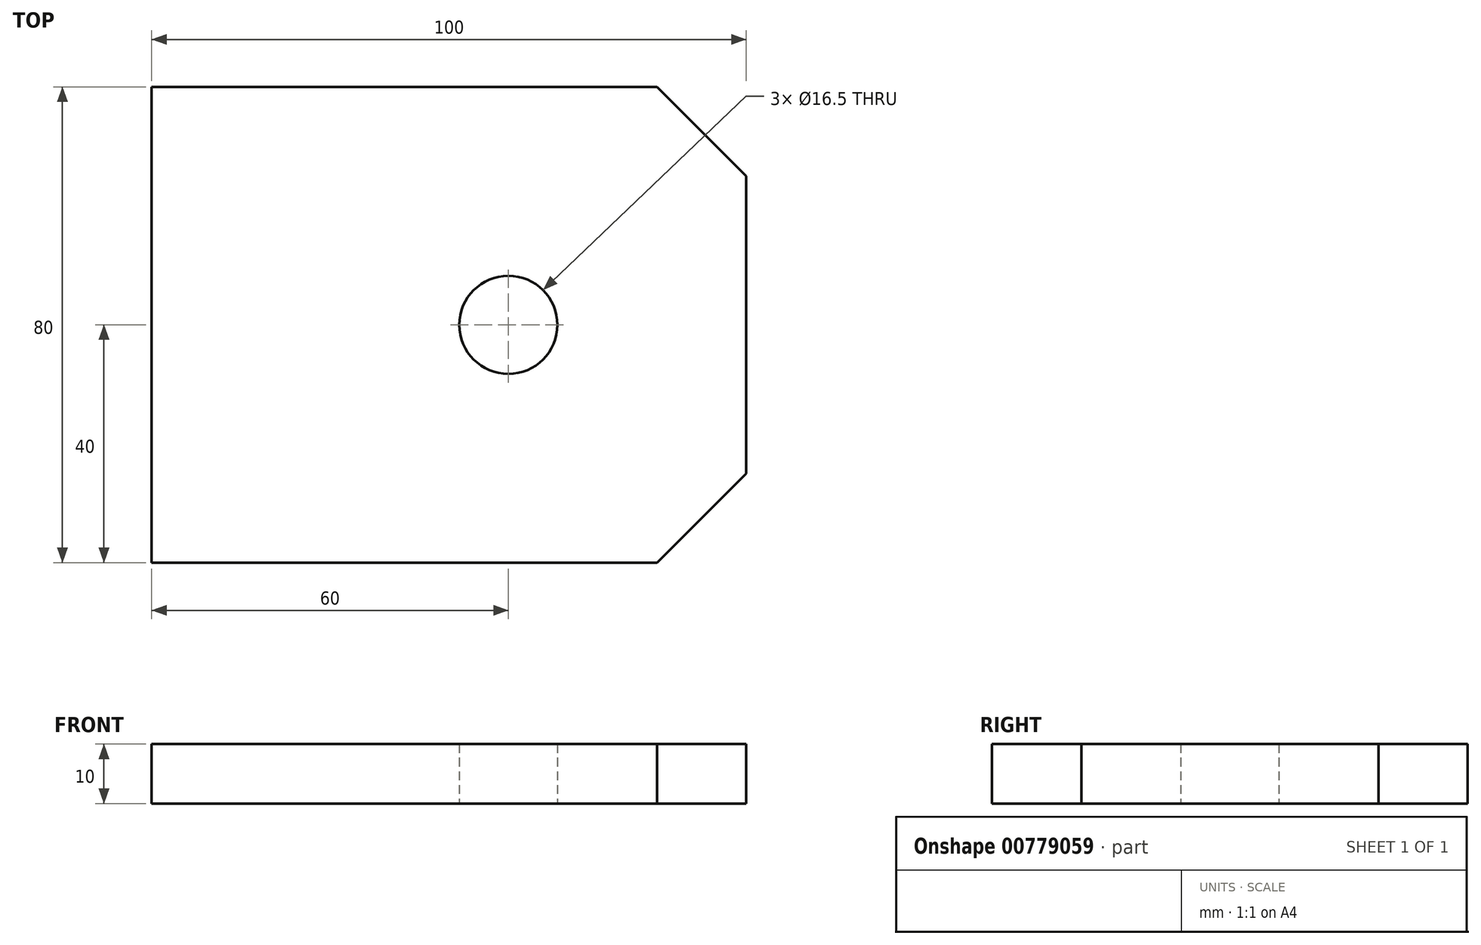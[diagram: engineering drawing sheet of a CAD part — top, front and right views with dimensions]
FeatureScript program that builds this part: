
annotation { "Feature Type Name" : "Feature", "Feature Type Description" : "" }
export const myFeature = defineFeature(function(context is Context, id is Id, definition is map)
    precondition{}
    {
        {
            var Q0;
            Q0=qCreatedBy(makeId("Top.planeOp"),FACE);
            var sketch = newSketch(context, id + "F0", { "sketchPlane" : qUnion([Q0])});
            skLineSegment(sketch, "E0", {"start": v(0, 0) * mm, "end": v(100, 0) * mm});
            skLineSegment(sketch, "E1", {"start": v(100, 0) * mm, "end": v(100, -80) * mm});
            skLineSegment(sketch, "E2", {"start": v(100, -80) * mm, "end": v(0, -80) * mm});
            skLineSegment(sketch, "E3", {"start": v(0, -80) * mm, "end": v(0, 0) * mm});
            skCircle(sketch, "E4", {"center": v(60, -40) * mm, "radius": 8.25 * mm});
            skSolve(sketch);
        }
        {
            var Q0;
            Q0=makeQuery(id+"F0.imprint","IMPRINT",FACE,{"disambiguationData":[TD([[makeQuery(id+"F0.imprint","IMPRINT",EDGE,{"derivedFrom":sQuery(id+"F0.wireOp",EDGE,"E0")}),-1.0]])]});
            extrude(context, id + "F1", {"entities" : qUnion([Q0]), "depth" : 10 * mm, "offsetDistance" : 25 * mm});
        }
        {
            var Q0;
            Q0=makeQuery(id+"F1.opExtrude","SWEPT_EDGE",EDGE,{"disambiguationData":[OSD([sQuery(id+"F0.wireOp",EDGE,"E0"),sQuery(id+"F0.wireOp",EDGE,"E1")])]});
            var Q1;
            Q1=makeQuery(id+"F1.opExtrude","SWEPT_EDGE",EDGE,{"disambiguationData":[OSD([sQuery(id+"F0.wireOp",EDGE,"E1"),sQuery(id+"F0.wireOp",EDGE,"E2")])]});
            chamfer(context, id + "F2", {"entities" : qUnion([Q0, Q1]), "width" : 15 * mm, "tangentPropagation" : true});
        }
    });
